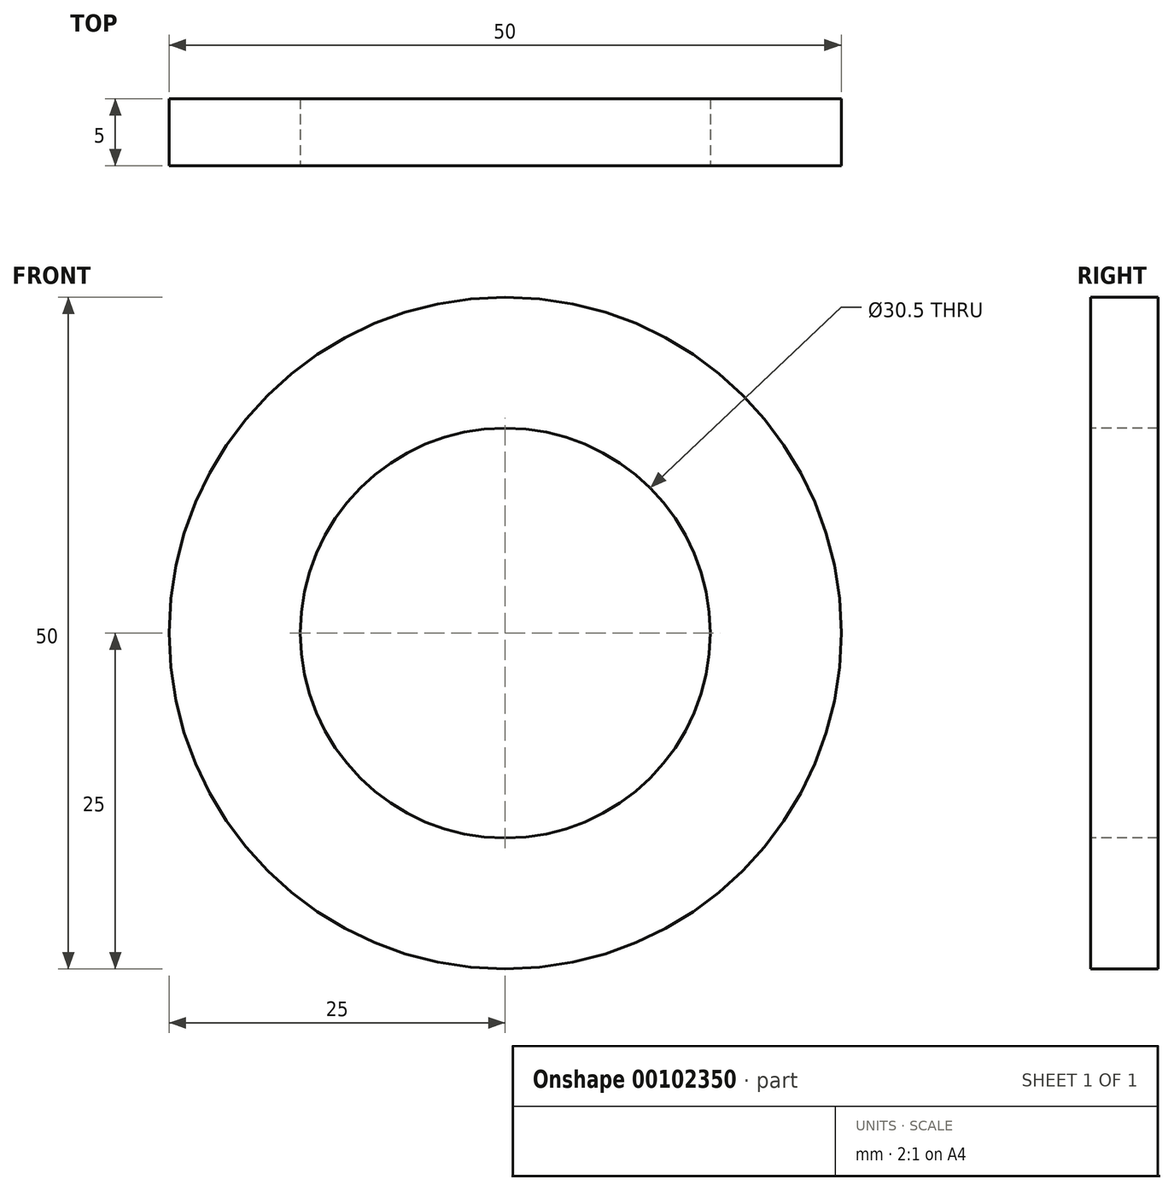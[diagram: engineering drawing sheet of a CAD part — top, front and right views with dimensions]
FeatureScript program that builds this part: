
annotation { "Feature Type Name" : "Feature", "Feature Type Description" : "" }
export const myFeature = defineFeature(function(context is Context, id is Id, definition is map)
    precondition{}
    {
        {
            var Q0;
            Q0=qCreatedBy(makeId("Front.planeOp"),FACE);
            var sketch = newSketch(context, id + "F0", { "sketchPlane" : qUnion([Q0])});
            skCircle(sketch, "E0", {"center": v(0, 0) * mm, "radius": 25 * mm});
            skCircle(sketch, "E1", {"center": v(0, 0) * mm, "radius": 15.25 * mm});
            skSolve(sketch);
        }
        {
            var Q0;
            Q0=makeQuery(id+"F0.imprint","IMPRINT",FACE,{"disambiguationData":[TD([[makeQuery(id+"F0.imprint","IMPRINT",EDGE,{"derivedFrom":sQuery(id+"F0.wireOp",EDGE,"E0")}),1.0]])]});
            extrude(context, id + "F1", {"entities" : qUnion([Q0]), "oppositeDirection" : true, "depth" : 5 * mm});
        }
    });
